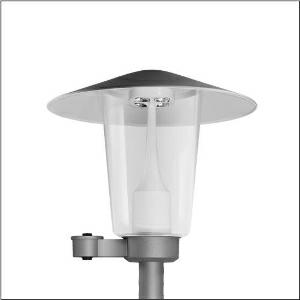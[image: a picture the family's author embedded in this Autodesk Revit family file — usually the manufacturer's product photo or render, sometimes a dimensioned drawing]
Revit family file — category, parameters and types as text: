
# Revit family: pilzleuchte_iq___st1_2a_5xa5235eu14h000022_6897
name_source: partatom
category: Lighting Fixtures
units: mm (PartAtom-declared; Revit-internal decimal feet)

## family parameters
Cut with Voids When Loaded = No
Host = Face
Light Source = No
Part Type = Normal
Room Calculation Point = No
Round Connector Dimension = Use Diameter
Shared = No

## types (1)
- --- (1 x LED, 1550 lm, 10.7 W, 3000K)
    Apparent Load = 11 VA
    CIE Flux Codes = 24 61 93 98 100
    Color Rendering = 70
    Color Temperature = 3000K
    Default Elevation = 1800 mm
    Description = Mushroom Luminaire iQ, mast luminaire, Module 540 iQ-SR, primary light control with 3 zone facetted reflector, of plastic, silver coated, highly specular, structured, primary optical cover: cover, of PMMA, transparent, light distribution: ST1.2a, light emission: direct distribution, primary light characteristic: asymmetric, installation type: post-top, LED, High Power LED, rated luminous flux: 1.550lm, luminous efficacy: 145lm/W, light colour: 730, colour temperature: 3000K, control gear: iQ-Street Remote, D4i with power reduction, control: optimised constant luminous flux control (CLO 2.0), Desk-Remote (wireless, voltage-free reading and setting of iQ features in the workshop via application-optimized NFC function/RFID function), Light-Fading, Smart-Wire, Night-Set, Lumen-Switch, Temp-Guard, Auto-Match, Street-Remote, pre-setting: logarithmic dimming characteristic, with terminal, 6-pole, max. 2.5mm², mains connection: 230..240V, AC, 50/60Hz, connection cable pre-assembled, cable length: 5,5m, wiring characteristics: H07RN-F, start of lifetime: 11W, end of service life: 11W, reduction: 6W, luminaire housing, upper part, of glass-fibre reinforced polyester, coated, SITECO metallic grey (DB 702S), diameter: 650mm, height: 586mm, spigot size: d x l = 76 x 70mm (post-top) | with reducer (optional accessory) 60 x 70mm, mounting height: 3..5m, post-top mast mounting element, of diecast aluminium, coated, SITECO metallic grey (DB 702S), Module 540 iQ-SR, traffic white (RAL 9016), equipment: standard, Smart Interface below, protection rating (complete): IP65, insulation class (complete): insulation class II (safety insulation), certification: CE, ENEC, VDE, packaging unit: 1 piece

Light Distribution: ST1.2a
    Height = 586 mm
    Lamp = 1 x LED
    Lamp Light Flux = 1550 lm
    Lamp Power = 10.7 W
    Lamp count = 1
    Length = 650 mm
    Luminous efficacy = 145 lm/W
    Manufacturer = Siteco
    ModVariant = No
    Model = 5XA5235EU14H000022
    Number of Poles = 1
    OnlyDefault = Yes
    Power Factor = 1
    Product Name = Pilzleuchte iQ | ST1.2a
    Product group = mast luminaire | pylon top
    ProductGroupID = 6100
    Protection Class = Protection class II
    Protection Degree = IP 65
    RLX_Detail_Level = 1
    RLX_Emergency_Light_Flux = 0 lm
    RLX_Emergency_Type = 0
    RLX_Emergency_Type_DB = No
    RlxData = <blob elided: 51837 chars, md5=b7cd8e76>
    Socket = socket
    Standby Power = 0 W
    System Light Flux = 1550 lm
    System Power = 11 W
    Type Comments = factory setting: luminous flux: 100 % | dim-lin: 254 | 419 mA
    Type Image = l_1006957.jpg
    URL = http://relux.com
    VarID = @adj_091235
    Voltage = 0 V
    Weight = 0.00 kg
    Width = 0 mm  [stored 0 ft]

note: [stored X ft] marks values corroborated as IEEE doubles in the binary element streams (Revit-internal decimal feet)

## geometry (parser evidence)
native form markers: Blend x4, Sweep x13
no freeform markers — native parametric forms only
